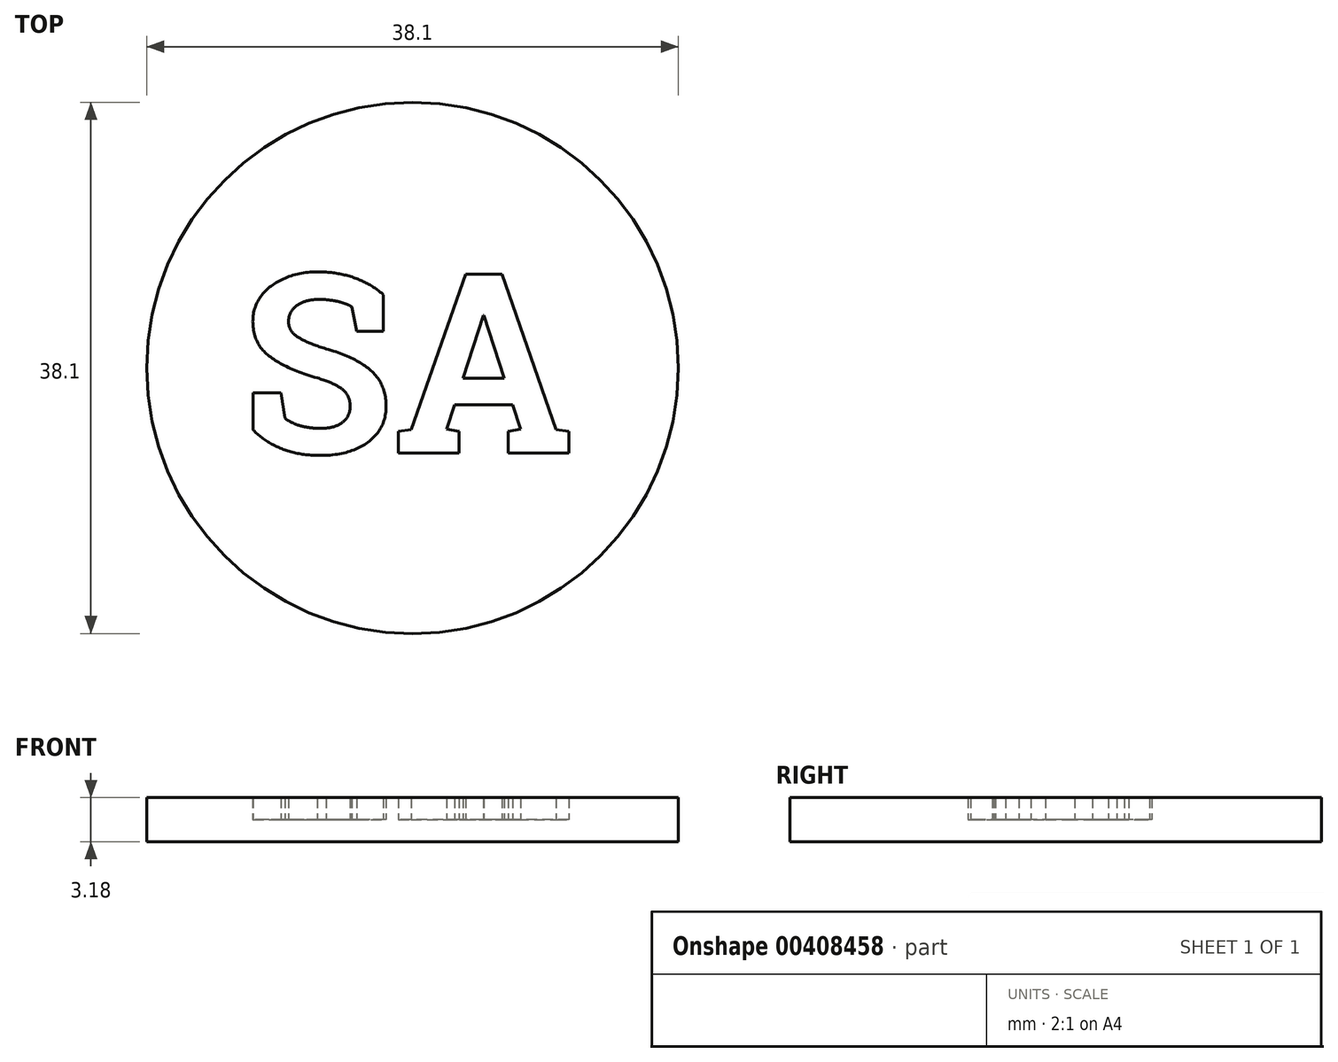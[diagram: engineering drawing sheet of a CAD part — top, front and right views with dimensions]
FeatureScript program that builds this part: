
annotation { "Feature Type Name" : "Feature", "Feature Type Description" : "" }
export const myFeature = defineFeature(function(context is Context, id is Id, definition is map)
    precondition{}
    {
        {
            var Q0;
            Q0=qCreatedBy(makeId("Front.planeOp"),FACE);
            var sketch = newSketch(context, id + "F0", { "sketchPlane" : qUnion([Q0])});
            skLineSegment(sketch, "E0.bottom", {"start": v(19.05, -1.59) * mm, "end": v(-19.05, -1.59) * mm});
            skLineSegment(sketch, "E0.top", {"start": v(19.05, 1.59) * mm, "end": v(-19.05, 1.59) * mm});
            skLineSegment(sketch, "E0.left", {"start": v(19.05, -1.59) * mm, "end": v(19.05, 1.59) * mm});
            skLineSegment(sketch, "E0.right", {"start": v(-19.05, -1.59) * mm, "end": v(-19.05, 1.59) * mm});
            skPoint(sketch, "E0.middle", {"position": v(0, 0) * mm});
            skLineSegment(sketch, "E1", {"start": v(0, 1.59) * mm, "end": v(0, -1.59) * mm});
            skSolve(sketch);
        }
        {
            var Q0;
            {var subQ0=sQuery(id+"F0.wireOp",EDGE,"E0.left");Q0=makeQuery(id+"F0.imprint","IMPRINT",FACE,{"disambiguationData":[TD([[makeQuery(id+"F0.imprint","IMPRINT",EDGE,{"derivedFrom":subQ0}),1.0]])]});}
            var Q1;
            Q1=sQuery(id+"F0.wireOp",EDGE,"E1");
            revolve(context, id + "F1", {"entities" : qUnion([Q0]), "axis" : qUnion([Q1]), "revolveType" : RevolveType.FULL});
        }
        {
            var Q0;
            Q0=qCreatedBy(makeId("Top.planeOp"),FACE);
            var sketch = newSketch(context, id + "F2", { "sketchPlane" : qUnion([Q0])});
            skText(sketch, "E2", { "text": "SA", "fontName": "RobotoSlab-Bold.ttf"});
            const initialGuessF2  = {"E2": [-0.0123, -0.00609, 1, 0, 0.01297]};
            skSetInitialGuess(sketch, initialGuessF2);
            skSolve(sketch);
        }
        {
            var Q0;
            Q0 = qSketchRegion(id + "F2", true);
            extrude(context, id + "F3", {"entities" : qUnion([Q0]), "operationType" : NewBodyOperationType.REMOVE, "depth" : 3.05 * mm});
        }
    });
